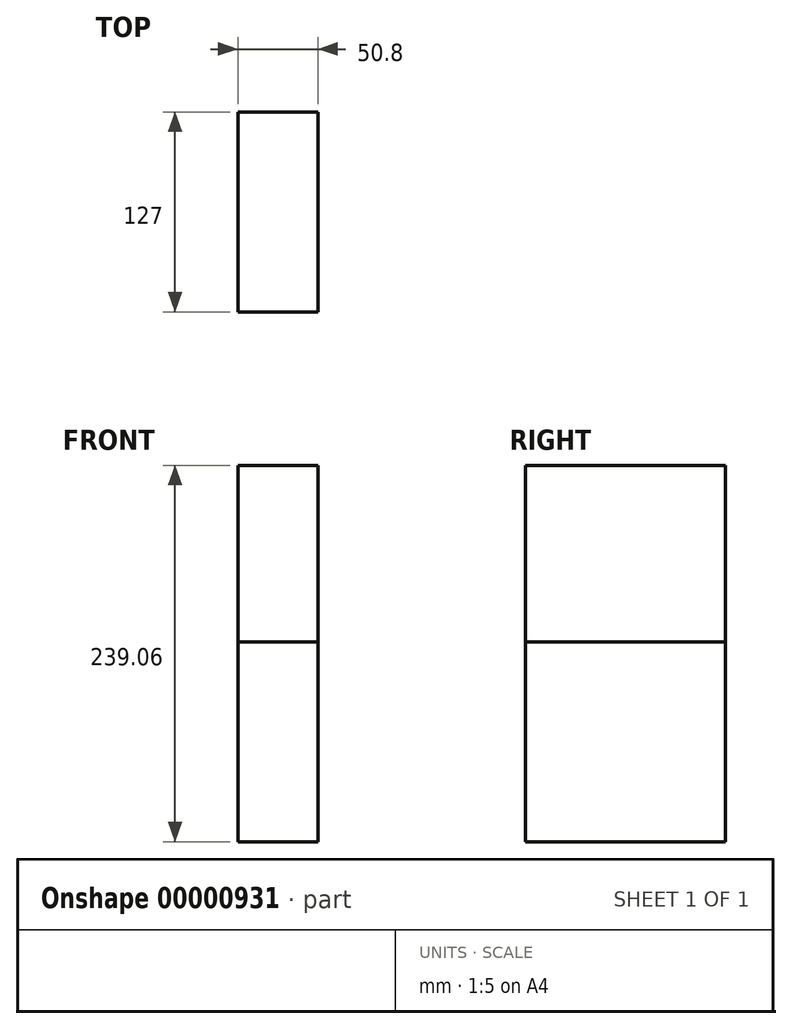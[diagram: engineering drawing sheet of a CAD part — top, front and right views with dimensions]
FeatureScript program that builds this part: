
annotation { "Feature Type Name" : "Feature", "Feature Type Description" : "" }
export const myFeature = defineFeature(function(context is Context, id is Id, definition is map)
    precondition{}
    {
        {
            var Q0;
            Q0=qCreatedBy(makeId("Top.planeOp"),FACE);
            var sketch = newSketch(context, id + "F0", { "sketchPlane" : qUnion([Q0])});
            skLineSegment(sketch, "E0.bottom", {"start": v(0, 0) * mm, "end": v(50.8, 0) * mm});
            skLineSegment(sketch, "E0.top", {"start": v(0, 127) * mm, "end": v(50.8, 127) * mm});
            skLineSegment(sketch, "E0.left", {"start": v(0, 0) * mm, "end": v(0, 127) * mm});
            skLineSegment(sketch, "E0.right", {"start": v(50.8, 0) * mm, "end": v(50.8, 127) * mm});
            skSolve(sketch);
        }
        {
            var Q0;
            Q0=makeQuery(id+"F0.imprint","IMPRINT",FACE,{"disambiguationData":[TD([[makeQuery(id+"F0.imprint","IMPRINT",EDGE,{"derivedFrom":sQuery(id+"F0.wireOp",EDGE,"E0.bottom")}),1.0]])]});
            extrude(context, id + "F1", {"entities" : qUnion([Q0]), "depth" : 127 * mm});
        }
        {
            var Q0;
            Q0=makeQuery(id+"F1.opExtrude","CAP_FACE",FACE,{"disambiguationData":[OSD([sQuery(id+"F0.wireOp",EDGE,"E0.bottom"),sQuery(id+"F0.wireOp",EDGE,"E0.top"),sQuery(id+"F0.wireOp",EDGE,"E0.left"),sQuery(id+"F0.wireOp",EDGE,"E0.right")])],"isStart":false});
            var sketch = newSketch(context, id + "F2", { "sketchPlane" : qUnion([Q0])});
            skSolve(sketch);
        }
        {
            var Q0;
            Q0 = qSketchRegion(id + "F2", true);
            var Q1;
            Q1=makeQuery(id+"F2.imprint","IMPRINT",FACE,{"disambiguationData":[TD([[makeQuery(id+"F2.imprint","IMPRINT",EDGE,{"derivedFrom":makeQuery(id+"F1.opExtrude","CAP_EDGE",EDGE,{"disambiguationData":[OSD([sQuery(id+"F0.wireOp",EDGE,"E0.bottom")])],"isStart":false})}),1.0]])]});
            extrude(context, id + "F3", {"entities" : qUnion([Q0, Q1]), "depth" : 112.06 * mm});
        }
    });
